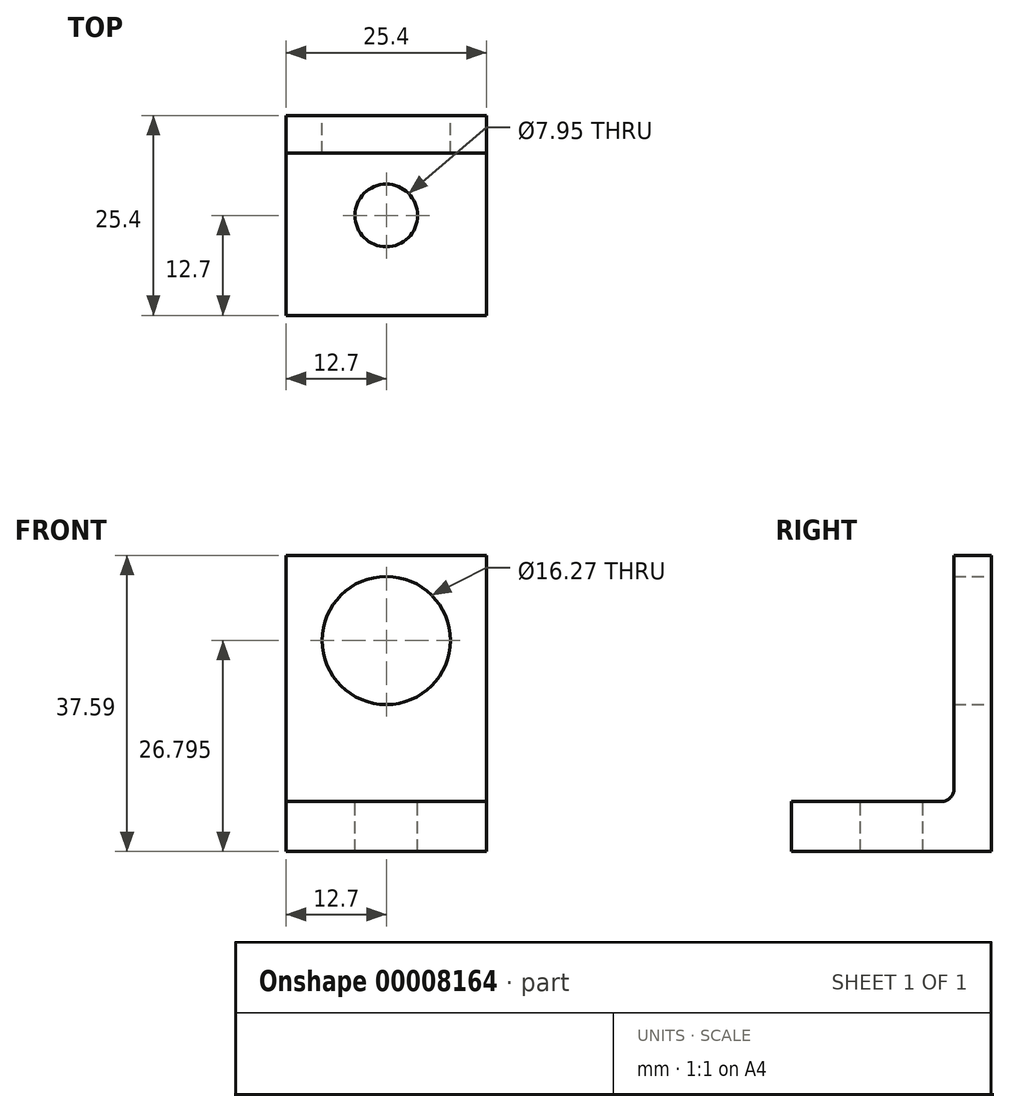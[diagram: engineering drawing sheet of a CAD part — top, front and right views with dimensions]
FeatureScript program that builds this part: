
annotation { "Feature Type Name" : "Feature", "Feature Type Description" : "" }
export const myFeature = defineFeature(function(context is Context, id is Id, definition is map)
    precondition{}
    {
        {
            var Q0;
            Q0=qCreatedBy(makeId("Top.planeOp"),FACE);
            var sketch = newSketch(context, id + "F0", { "sketchPlane" : qUnion([Q0])});
            skLineSegment(sketch, "E0.rect.bottom", {"start": v(12.7, -12.7) * mm, "end": v(-12.7, -12.7) * mm});
            skLineSegment(sketch, "E0.rect.top", {"start": v(12.7, 12.7) * mm, "end": v(-12.7, 12.7) * mm});
            skLineSegment(sketch, "E0.rect.left", {"start": v(12.7, -12.7) * mm, "end": v(12.7, 12.7) * mm});
            skLineSegment(sketch, "E0.rect.right", {"start": v(-12.7, -12.7) * mm, "end": v(-12.7, 12.7) * mm});
            skPoint(sketch, "E0.rect.middle", {"position": v(0, 0) * mm});
            skSolve(sketch);
        }
        {
            var Q0;
            Q0=qSketchRegion(id+"F0",true);
            extrude(context, id + "F1", {"entities" : qUnion([Q0]), "oppositeDirection" : true, "depth" : 37.6 * mm});
        }
        {
            var Q0;
            Q0=makeQuery(id+"F1.opExtrude","SWEPT_FACE",FACE,{"disambiguationData":[OSD([sQuery(id+"F0.wireOp",EDGE,"E0.rect.right")])]});
            var sketch = newSketch(context, id + "F2", { "sketchPlane" : qUnion([Q0])});
            skLineSegment(sketch, "E1.bottom", {"start": v(-7.94, 0) * mm, "end": v(12.7, 0) * mm});
            skLineSegment(sketch, "E1.top", {"start": v(-7.94, -31.24) * mm, "end": v(12.7, -31.24) * mm});
            skLineSegment(sketch, "E1.left", {"start": v(-7.94, 0) * mm, "end": v(-7.94, -31.24) * mm});
            skLineSegment(sketch, "E1.right", {"start": v(12.7, 0) * mm, "end": v(12.7, -31.24) * mm});
            skSolve(sketch);
        }
        {
            var Q0;
            Q0 = qSketchRegion(id + "F2", true);
            var Q1;
            Q1=makeQuery(id+"F1.opExtrude","SWEPT_FACE",FACE,{"disambiguationData":[OSD([sQuery(id+"F0.wireOp",EDGE,"E0.rect.left")])]});
            extrude(context, id + "F3", {"entities" : qUnion([Q0]), "operationType" : NewBodyOperationType.REMOVE, "endBound" : BoundingType.UP_TO_SURFACE, "oppositeDirection" : true, "endBoundEntityFace" : qUnion([Q1]), "depth" : 25.4 * mm});
        }
        {
            var Q0;
            Q0=makeQuery(id+"F1.opExtrude","SWEPT_FACE",FACE,{"disambiguationData":[OSD([sQuery(id+"F0.wireOp",EDGE,"E0.rect.top")])]});
            var sketch = newSketch(context, id + "F4", { "sketchPlane" : qUnion([Q0])});
            skCircle(sketch, "E2", {"center": v(0, -10.8) * mm, "radius": 8.14 * mm});
            skSolve(sketch);
        }
        {
            var Q0;
            Q0 = qSketchRegion(id + "F4", true);
            var Q1;
            Q1=makeQuery(id+"F3.boolean.opBoolean","COPY",FACE,{"derivedFrom":makeQuery(id+"F3.opExtrude","SWEPT_FACE",FACE,{"disambiguationData":[OSD([sQuery(id+"F2.wireOp",EDGE,"E1.left")])]})});
            extrude(context, id + "F5", {"entities" : qUnion([Q0]), "operationType" : NewBodyOperationType.REMOVE, "endBound" : BoundingType.UP_TO_SURFACE, "oppositeDirection" : true, "endBoundEntityFace" : qUnion([Q1]), "depth" : 25.4 * mm});
        }
        {
            var Q0;
            Q0=makeQuery(id+"F1.opExtrude","SWEPT_FACE",FACE,{"disambiguationData":[OSD([sQuery(id+"F0.wireOp",EDGE,"E0.rect.right")])]});
            var sketch = newSketch(context, id + "F6", { "sketchPlane" : qUnion([Q0])});
            skLineSegment(sketch, "E3.bottom", {"start": v(-7.94, -1.27) * mm, "end": v(4.7, -1.27) * mm, "construction": true});
            skLineSegment(sketch, "E3.top", {"start": v(-7.94, -20.32) * mm, "end": v(4.7, -20.32) * mm, "construction": true});
            skLineSegment(sketch, "E3.left", {"start": v(-7.94, -1.27) * mm, "end": v(-7.94, -20.32) * mm, "construction": true});
            skLineSegment(sketch, "E3.right", {"start": v(4.7, -1.27) * mm, "end": v(4.7, -20.32) * mm, "construction": true});
            skLineSegment(sketch, "E4", {"start": v(-7.94, -1.27) * mm, "end": v(-7.94, -20.32) * mm});
            skLineSegment(sketch, "E5", {"start": v(4.7, -10.8) * mm, "end": v(-16.46, -10.8) * mm, "construction": true});
            skLineSegment(sketch, "E6", {"start": v(12.7, -23.75) * mm, "end": v(-17.39, -23.75) * mm, "construction": true});
            skSolve(sketch);
        }
        {
            var Q0;
            Q0=makeQuery(id+"F3.boolean.opBoolean","COPY",FACE,{"derivedFrom":makeQuery(id+"F3.opExtrude","SWEPT_FACE",FACE,{"disambiguationData":[OSD([sQuery(id+"F2.wireOp",EDGE,"E1.top")])]})});
            var sketch = newSketch(context, id + "F7", { "sketchPlane" : qUnion([Q0])});
            skCircle(sketch, "E7", {"center": v(0, 0) * mm, "radius": 3.98 * mm});
            skSolve(sketch);
        }
        {
            var Q0;
            Q0 = qSketchRegion(id + "F7", true);
            var Q1;
            Q1=makeQuery(id+"F1.opExtrude","CAP_FACE",FACE,{"disambiguationData":[OSD([sQuery(id+"F0.wireOp",EDGE,"E0.rect.bottom"),sQuery(id+"F0.wireOp",EDGE,"E0.rect.top"),sQuery(id+"F0.wireOp",EDGE,"E0.rect.left"),sQuery(id+"F0.wireOp",EDGE,"E0.rect.right")])],"isStart":false});
            extrude(context, id + "F8", {"entities" : qUnion([Q0]), "operationType" : NewBodyOperationType.REMOVE, "endBound" : BoundingType.UP_TO_SURFACE, "oppositeDirection" : true, "endBoundEntityFace" : qUnion([Q1]), "depth" : 25.4 * mm});
        }
        {
            var Q0;
            Q0=makeQuery(id+"F3.boolean.opBoolean","COPY",EDGE,{"derivedFrom":makeQuery(id+"F3.opExtrude","SWEPT_EDGE",EDGE,{"disambiguationData":[OSD([sQuery(id+"F2.wireOp",EDGE,"E1.top"),sQuery(id+"F2.wireOp",EDGE,"E1.left")])]})});
            fillet(context, id + "F9", {"entities" : qUnion([Q0]), "radius" : 1.59 * mm, "tangentPropagation" : true, "allowEdgeOverflow" : false});
        }
    });
